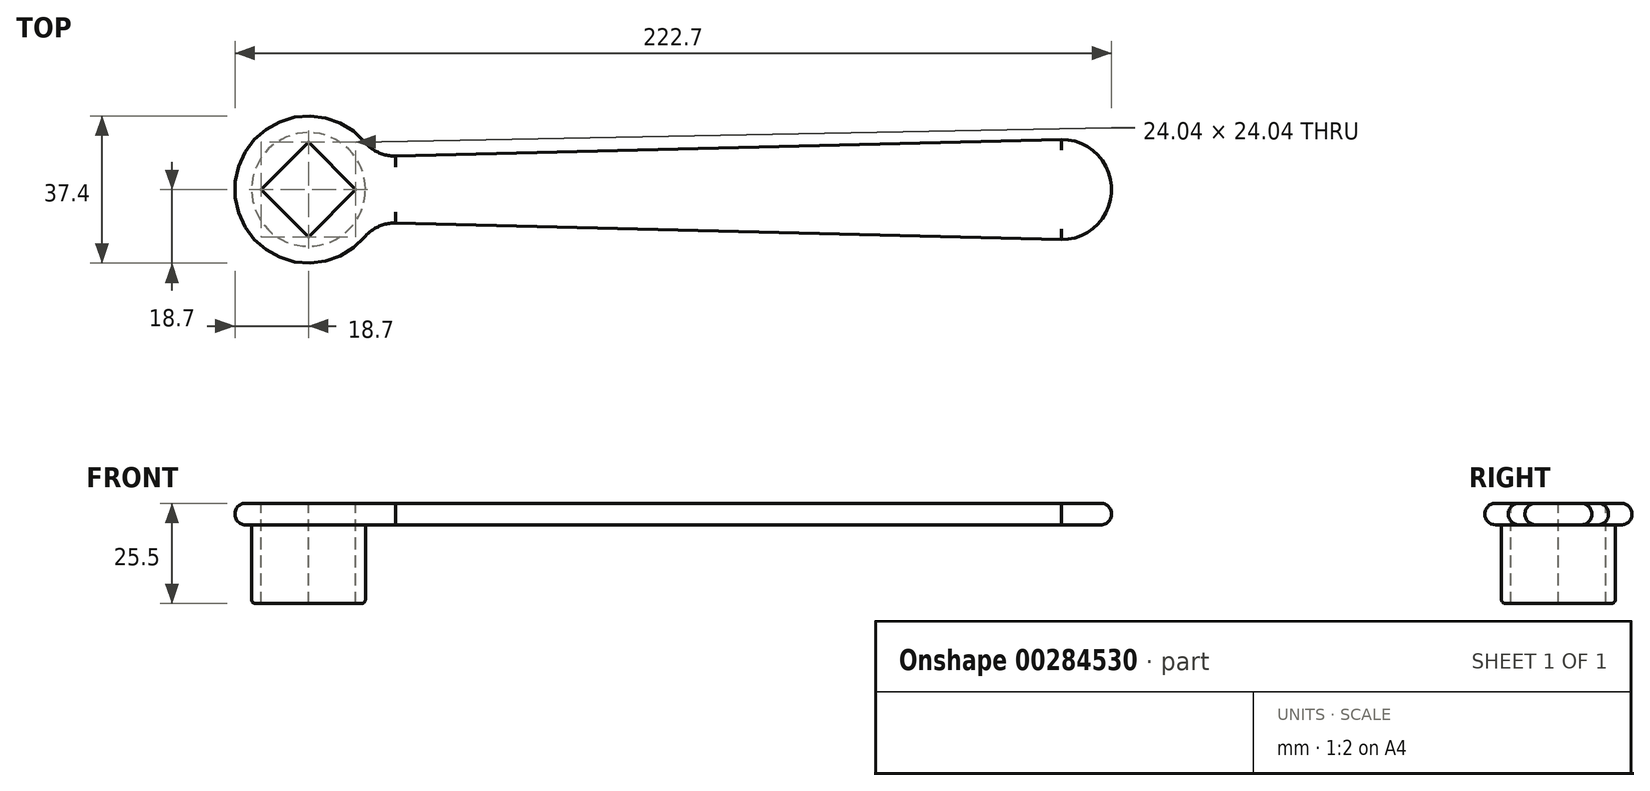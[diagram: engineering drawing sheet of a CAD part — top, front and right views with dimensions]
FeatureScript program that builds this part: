
annotation { "Feature Type Name" : "Feature", "Feature Type Description" : "" }
export const myFeature = defineFeature(function(context is Context, id is Id, definition is map)
    precondition{}
    {
        {
            var Q0;
            Q0=qCreatedBy(makeId("Top.planeOp"),FACE);
            var sketch = newSketch(context, id + "F0", { "sketchPlane" : qUnion([Q0])});
            skArc(sketch, "E0", {"start": v(14.3, 12.05) * mm, "mid": v(-18.7, 0) * mm, "end": v(14.3, -12.05) * mm});
            skLineSegment(sketch, "E1", {"start": v(22.1, 8.5) * mm, "end": v(22.1, -8.5) * mm, "construction": true});
            skPoint(sketch, "E2", {"position": v(204, 0) * mm});
            skPoint(sketch, "E2.positionSnap0", {"position": v(22.1, 0) * mm});
            skPoint(sketch, "E3", {"position": v(191.25, 0) * mm});
            skArc(sketch, "E4", {"start": v(191.25, 12.75) * mm, "mid": v(204, 0) * mm, "end": v(191.25, -12.75) * mm});
            skLineSegment(sketch, "E5", {"start": v(191.25, 12.75) * mm, "end": v(22.1, 8.5) * mm});
            skLineSegment(sketch, "E6", {"start": v(191.25, -12.75) * mm, "end": v(22.1, -8.5) * mm});
            skArc(sketch, "E7", {"start": v(22.1, 8.5) * mm, "mid": v(17.8, 9.4) * mm, "end": v(14.3, 12.05) * mm});
            skArc(sketch, "E8.MirrorCS", {"start": v(22.1, -8.5) * mm, "mid": v(17.8, -9.4) * mm, "end": v(14.3, -12.05) * mm});
            skLineSegment(sketch, "E9", {"start": v(-12.02, 0) * mm, "end": v(0, 12.02) * mm, "construction": true});
            skLineSegment(sketch, "E10", {"start": v(0, 12.02) * mm, "end": v(12.02, 0) * mm, "construction": true});
            skLineSegment(sketch, "E11", {"start": v(12.02, 0) * mm, "end": v(0, -12.02) * mm, "construction": true});
            skLineSegment(sketch, "E12", {"start": v(0, -12.02) * mm, "end": v(-12.02, 0) * mm, "construction": true});
            skSolve(sketch);
        }
        {
            var Q0;
            Q0=makeQuery(id+"F0.imprint","IMPRINT",FACE,{"disambiguationData":[TD([[makeQuery(id+"F0.imprint","IMPRINT",EDGE,{"derivedFrom":sQuery(id+"F0.wireOp",EDGE,"E0")}),1.0]])]});
            var Q1;
            Q1=sQuery(id+"F0.wireOp",EDGE,"E0");
            var Q2;
            Q2=sQuery(id+"F0.wireOp",EDGE,"E7");
            var Q3;
            Q3=sQuery(id+"F0.wireOp",EDGE,"E4");
            var Q4;
            Q4=sQuery(id+"F0.wireOp",EDGE,"E8.MirrorCS");
            var Q5;
            Q5=sQuery(id+"F0.wireOp",EDGE,"E6");
            var Q6;
            Q6=sQuery(id+"F0.wireOp",EDGE,"E5");
            extrude(context, id + "F1", {"entities" : qUnion([Q0]), "surfaceEntities" : qUnion([Q1, Q2, Q3, Q4, Q5, Q6]), "oppositeDirection" : true, "depth" : 5.5 * mm});
        }
        {
            var Q0;
            Q0=makeQuery(id+"F1.opExtrude","CAP_FACE",FACE,{"disambiguationData":[OSD([sQuery(id+"F0.wireOp",EDGE,"E0"),sQuery(id+"F0.wireOp",EDGE,"E4"),sQuery(id+"F0.wireOp",EDGE,"E5"),sQuery(id+"F0.wireOp",EDGE,"E6"),sQuery(id+"F0.wireOp",EDGE,"E7"),sQuery(id+"F0.wireOp",EDGE,"E8.MirrorCS")])],"isStart":true});
            var Q1;
            Q1=makeQuery(id+"F1.opExtrude","CAP_FACE",FACE,{"disambiguationData":[OSD([sQuery(id+"F0.wireOp",EDGE,"E0"),sQuery(id+"F0.wireOp",EDGE,"E4"),sQuery(id+"F0.wireOp",EDGE,"E5"),sQuery(id+"F0.wireOp",EDGE,"E6"),sQuery(id+"F0.wireOp",EDGE,"E7"),sQuery(id+"F0.wireOp",EDGE,"E8.MirrorCS")])],"isStart":false});
            fillet(context, id + "F2", {"entities" : qUnion([Q0, Q1]), "radius" : 2.75 * mm, "tangentPropagation" : true, "allowEdgeOverflow" : false});
        }
        {
            var Q0;
            Q0=qCreatedBy(makeId("Top.planeOp"),FACE);
            var sketch = newSketch(context, id + "F3", { "sketchPlane" : qUnion([Q0])});
            skCircle(sketch, "E13", {"center": v(0, 0) * mm, "radius": 14.45 * mm});
            skSolve(sketch);
        }
        {
            var Q0;
            Q0 = qSketchRegion(id + "F3", true);
            extrude(context, id + "F4", {"entities" : qUnion([Q0]), "operationType" : NewBodyOperationType.ADD, "oppositeDirection" : true, "depth" : 25.5 * mm});
        }
        {
            var Q0;
            Q0=makeQuery(id+"F4.opExtrude","CAP_EDGE",EDGE,{"disambiguationData":[OSD([sQuery(id+"F3.wireOp",EDGE,"E13")])],"isStart":false});
            fillet(context, id + "F5", {"entities" : qUnion([Q0]), "radius" : 1 * mm, "tangentPropagation" : true, "allowEdgeOverflow" : false});
        }
        {
            var Q0;
            Q0=makeQuery(id+"F1.opExtrude","CAP_FACE",FACE,{"disambiguationData":[OSD([sQuery(id+"F0.wireOp",EDGE,"E0"),sQuery(id+"F0.wireOp",EDGE,"E4"),sQuery(id+"F0.wireOp",EDGE,"E5"),sQuery(id+"F0.wireOp",EDGE,"E6"),sQuery(id+"F0.wireOp",EDGE,"E7"),sQuery(id+"F0.wireOp",EDGE,"E8.MirrorCS")])],"isStart":true});
            var sketch = newSketch(context, id + "F6", { "sketchPlane" : qUnion([Q0])});
            skLineSegment(sketch, "E14.0", {"start": v(-12.02, 0) * mm, "end": v(0, 12.02) * mm});
            skLineSegment(sketch, "E14.1", {"start": v(0, 12.02) * mm, "end": v(12.02, 0) * mm});
            skLineSegment(sketch, "E14.2", {"start": v(12.02, 0) * mm, "end": v(0, -12.02) * mm});
            skLineSegment(sketch, "E14.3", {"start": v(0, -12.02) * mm, "end": v(-12.02, 0) * mm});
            skSolve(sketch);
        }
        {
            var Q0;
            Q0=makeQuery(id+"F6.imprint","IMPRINT",FACE,{"disambiguationData":[TD([[makeQuery(id+"F6.imprint","IMPRINT",EDGE,{"derivedFrom":sQuery(id+"F6.wireOp",EDGE,"E14.0")}),-1.0]])]});
            extrude(context, id + "F7", {"entities" : qUnion([Q0]), "operationType" : NewBodyOperationType.REMOVE, "endBound" : BoundingType.THROUGH_ALL, "oppositeDirection" : true, "depth" : 25 * mm});
        }
    });
